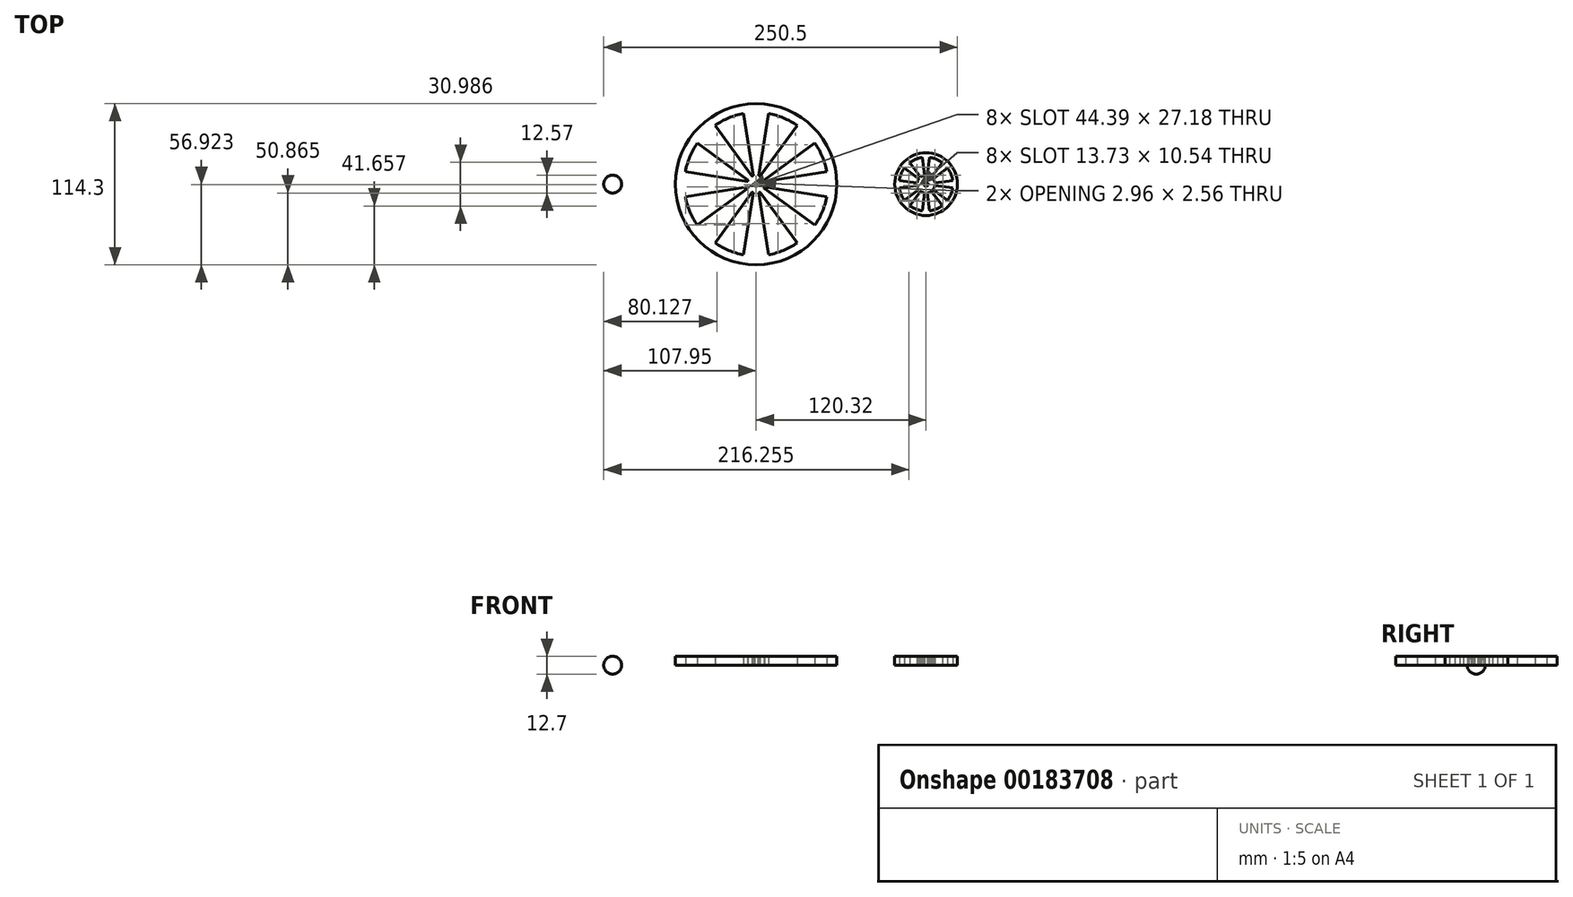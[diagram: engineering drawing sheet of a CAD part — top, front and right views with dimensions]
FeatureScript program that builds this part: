
annotation { "Feature Type Name" : "Feature", "Feature Type Description" : "" }
export const myFeature = defineFeature(function(context is Context, id is Id, definition is map)
    precondition{}
    {
        {
            var Q0;
            Q0=qCreatedBy(makeId("Top.planeOp"),FACE);
            var sketch = newSketch(context, id + "F0", { "sketchPlane" : qUnion([Q0])});
            skCircle(sketch, "E0", {"center": v(0, 0) * mm, "radius": 1.5 * mm});
            skCircle(sketch, "E1", {"center": v(0, 0) * mm, "radius": 57.15 * mm});
            skCircle(sketch, "E2", {"center": v(0, 0) * mm, "radius": 6.35 * mm});
            skCircle(sketch, "E3", {"center": v(0, 0) * mm, "radius": 50.8 * mm});
            skLineSegment(sketch, "E4", {"start": v(0, 6.35) * mm, "end": v(0, 50.8) * mm, "construction": true});
            skLineSegment(sketch, "E5", {"start": v(-1.9, 6.06) * mm, "end": v(-8.9, 50.02) * mm});
            skLineSegment(sketch, "E6", {"start": v(8.89, 50.02) * mm, "end": v(1.9, 6.06) * mm});
            skLineSegment(sketch, "E7.1.0", {"start": v(-29.08, 41.65) * mm, "end": v(-2.94, 5.63) * mm});
            skLineSegment(sketch, "E7.1.1", {"start": v(-5.63, 2.94) * mm, "end": v(-41.65, 29.08) * mm});
            skLineSegment(sketch, "E7.2.0", {"start": v(-50.02, 8.9) * mm, "end": v(-6.06, 1.9) * mm});
            skLineSegment(sketch, "E7.2.1", {"start": v(-6.06, -1.9) * mm, "end": v(-50.02, -8.9) * mm});
            skLineSegment(sketch, "E7.3.0", {"start": v(-41.65, -29.08) * mm, "end": v(-5.63, -2.94) * mm});
            skLineSegment(sketch, "E7.3.1", {"start": v(-2.94, -5.63) * mm, "end": v(-29.08, -41.65) * mm});
            skLineSegment(sketch, "E7.4.0", {"start": v(-8.9, -50.02) * mm, "end": v(-1.9, -6.06) * mm});
            skLineSegment(sketch, "E7.4.1", {"start": v(1.9, -6.06) * mm, "end": v(8.9, -50.02) * mm});
            skLineSegment(sketch, "E7.5.0", {"start": v(29.08, -41.65) * mm, "end": v(2.94, -5.63) * mm});
            skLineSegment(sketch, "E7.5.1", {"start": v(5.63, -2.94) * mm, "end": v(41.65, -29.08) * mm});
            skLineSegment(sketch, "E7.6.0", {"start": v(50.02, -8.9) * mm, "end": v(6.06, -1.9) * mm});
            skLineSegment(sketch, "E7.6.1", {"start": v(6.06, 1.9) * mm, "end": v(50.02, 8.9) * mm});
            skLineSegment(sketch, "E7.7.0", {"start": v(41.65, 29.08) * mm, "end": v(5.63, 2.94) * mm});
            skLineSegment(sketch, "E7.7.1", {"start": v(2.94, 5.63) * mm, "end": v(29.08, 41.65) * mm});
            skCircle(sketch, "E8", {"center": v(120.32, 0) * mm, "radius": 6.35 * mm});
            skCircle(sketch, "E9", {"center": v(120.32, 0) * mm, "radius": 1.5 * mm});
            skCircle(sketch, "E10", {"center": v(120.32, 0) * mm, "radius": 22.23 * mm});
            skCircle(sketch, "E11", {"center": v(120.32, 0) * mm, "radius": 19.05 * mm});
            skLineSegment(sketch, "E12", {"start": v(120.32, 6.35) * mm, "end": v(120.32, 19.05) * mm, "construction": true});
            skLineSegment(sketch, "E13", {"start": v(121.34, 6.27) * mm, "end": v(122.86, 18.88) * mm});
            skLineSegment(sketch, "E14", {"start": v(119.3, 6.27) * mm, "end": v(117.78, 18.88) * mm});
            skLineSegment(sketch, "E15.1.0", {"start": v(116.6, 5.15) * mm, "end": v(108.77, 15.15) * mm});
            skLineSegment(sketch, "E15.1.1", {"start": v(115.17, 3.71) * mm, "end": v(105.17, 11.55) * mm});
            skLineSegment(sketch, "E15.2.0", {"start": v(114.05, 1.02) * mm, "end": v(101.44, 2.54) * mm});
            skLineSegment(sketch, "E15.2.1", {"start": v(114.05, -1.02) * mm, "end": v(101.44, -2.54) * mm});
            skLineSegment(sketch, "E15.3.0", {"start": v(115.17, -3.71) * mm, "end": v(105.17, -11.55) * mm});
            skLineSegment(sketch, "E15.3.1", {"start": v(116.6, -5.15) * mm, "end": v(108.77, -15.15) * mm});
            skLineSegment(sketch, "E15.4.0", {"start": v(119.3, -6.27) * mm, "end": v(117.78, -18.88) * mm});
            skLineSegment(sketch, "E15.4.1", {"start": v(121.34, -6.27) * mm, "end": v(122.86, -18.88) * mm});
            skLineSegment(sketch, "E15.5.0", {"start": v(124.03, -5.15) * mm, "end": v(131.87, -15.15) * mm});
            skLineSegment(sketch, "E15.5.1", {"start": v(125.47, -3.71) * mm, "end": v(135.47, -11.55) * mm});
            skLineSegment(sketch, "E15.6.0", {"start": v(126.59, -1.02) * mm, "end": v(139.2, -2.54) * mm});
            skLineSegment(sketch, "E15.6.1", {"start": v(126.59, 1.02) * mm, "end": v(139.2, 2.54) * mm});
            skLineSegment(sketch, "E15.7.0", {"start": v(125.47, 3.71) * mm, "end": v(135.47, 11.55) * mm});
            skLineSegment(sketch, "E15.7.1", {"start": v(124.03, 5.15) * mm, "end": v(131.87, 15.15) * mm});
            skLineSegment(sketch, "E16", {"start": v(-1.08, 1.05) * mm, "end": v(1.08, 1.05) * mm});
            skPoint(sketch, "E17", {"position": v(0, 1.5) * mm});
            skLineSegment(sketch, "E18", {"start": v(119.24, 1.05) * mm, "end": v(121.4, 1.05) * mm});
            skPoint(sketch, "E19", {"position": v(120.32, 1.5) * mm});
            skCircle(sketch, "E20", {"center": v(-101.6, 0) * mm, "radius": 6.35 * mm});
            skLineSegment(sketch, "E21", {"start": v(-107.95, 0) * mm, "end": v(-95.25, 0) * mm});
            skSolve(sketch);
        }
        {
            var Q0;
            Q0=makeQuery(id+"F0.imprint","IMPRINT",FACE,{"disambiguationData":[TD([[makeQuery(id+"F0.imprint","IMPRINT",EDGE,{"derivedFrom":sQuery(id+"F0.wireOp",EDGE,"E1")}),1.0]])]});
            var Q1;
            {var subQ0=sQuery(id+"F0.wireOp",EDGE,"E7.1.1");var subQ1=sQuery(id+"F0.wireOp",EDGE,"E2");var subQ2=makeQuery(id+"F0.imprint","INTERSECT",VERTEX,{"derivedFrom":[subQ1,subQ0]});Q1=makeQuery(id+"F0.imprint","IMPRINT",FACE,{"disambiguationData":[TD([[makeQuery(id+"F0.imprint","IMPRINT",EDGE,{"disambiguationData":[TD([[subQ2,1.0]])],"derivedFrom":subQ1}),-1.0]])]});}
            var Q2;
            Q2=makeQuery(id+"F0.imprint","IMPRINT",FACE,{"disambiguationData":[TD([[makeQuery(id+"F0.imprint","IMPRINT",EDGE,{"derivedFrom":sQuery(id+"F0.wireOp",EDGE,"E0")}),-1.0]])]});
            var Q3;
            {var subQ0=sQuery(id+"F0.wireOp",EDGE,"E5");var subQ1=sQuery(id+"F0.wireOp",EDGE,"E2");var subQ2=makeQuery(id+"F0.imprint","INTERSECT",VERTEX,{"derivedFrom":[subQ1,subQ0]});Q3=makeQuery(id+"F0.imprint","IMPRINT",FACE,{"disambiguationData":[TD([[makeQuery(id+"F0.imprint","IMPRINT",EDGE,{"disambiguationData":[TD([[subQ2,1.0]])],"derivedFrom":subQ1}),-1.0]])]});}
            var Q4;
            {var subQ0=sQuery(id+"F0.wireOp",EDGE,"E6");var subQ1=sQuery(id+"F0.wireOp",EDGE,"E2");var subQ2=makeQuery(id+"F0.imprint","INTERSECT",VERTEX,{"derivedFrom":[subQ1,subQ0]});Q4=makeQuery(id+"F0.imprint","IMPRINT",FACE,{"disambiguationData":[TD([[makeQuery(id+"F0.imprint","IMPRINT",EDGE,{"disambiguationData":[TD([[subQ2,-1.0]])],"derivedFrom":subQ1}),-1.0]])]});}
            var Q5;
            {var subQ0=sQuery(id+"F0.wireOp",EDGE,"E7.6.1");var subQ1=sQuery(id+"F0.wireOp",EDGE,"E2");var subQ2=makeQuery(id+"F0.imprint","INTERSECT",VERTEX,{"derivedFrom":[subQ1,subQ0]});Q5=makeQuery(id+"F0.imprint","IMPRINT",FACE,{"disambiguationData":[TD([[makeQuery(id+"F0.imprint","IMPRINT",EDGE,{"disambiguationData":[TD([[subQ2,1.0]])],"derivedFrom":subQ1}),-1.0]])]});}
            var Q6;
            {var subQ0=sQuery(id+"F0.wireOp",EDGE,"E7.5.1");var subQ1=sQuery(id+"F0.wireOp",EDGE,"E2");var subQ2=makeQuery(id+"F0.imprint","INTERSECT",VERTEX,{"derivedFrom":[subQ1,subQ0]});Q6=makeQuery(id+"F0.imprint","IMPRINT",FACE,{"disambiguationData":[TD([[makeQuery(id+"F0.imprint","IMPRINT",EDGE,{"disambiguationData":[TD([[subQ2,1.0]])],"derivedFrom":subQ1}),-1.0]])]});}
            var Q7;
            {var subQ0=sQuery(id+"F0.wireOp",EDGE,"E7.4.1");var subQ1=sQuery(id+"F0.wireOp",EDGE,"E2");var subQ2=makeQuery(id+"F0.imprint","INTERSECT",VERTEX,{"derivedFrom":[subQ1,subQ0]});Q7=makeQuery(id+"F0.imprint","IMPRINT",FACE,{"disambiguationData":[TD([[makeQuery(id+"F0.imprint","IMPRINT",EDGE,{"disambiguationData":[TD([[subQ2,1.0]])],"derivedFrom":subQ1}),-1.0]])]});}
            var Q8;
            {var subQ0=sQuery(id+"F0.wireOp",EDGE,"E7.3.1");var subQ1=sQuery(id+"F0.wireOp",EDGE,"E2");var subQ2=makeQuery(id+"F0.imprint","INTERSECT",VERTEX,{"derivedFrom":[subQ1,subQ0]});Q8=makeQuery(id+"F0.imprint","IMPRINT",FACE,{"disambiguationData":[TD([[makeQuery(id+"F0.imprint","IMPRINT",EDGE,{"disambiguationData":[TD([[subQ2,1.0]])],"derivedFrom":subQ1}),-1.0]])]});}
            var Q9;
            {var subQ0=sQuery(id+"F0.wireOp",EDGE,"E7.2.1");var subQ1=sQuery(id+"F0.wireOp",EDGE,"E2");var subQ2=makeQuery(id+"F0.imprint","INTERSECT",VERTEX,{"derivedFrom":[subQ1,subQ0]});Q9=makeQuery(id+"F0.imprint","IMPRINT",FACE,{"disambiguationData":[TD([[makeQuery(id+"F0.imprint","IMPRINT",EDGE,{"disambiguationData":[TD([[subQ2,1.0]])],"derivedFrom":subQ1}),-1.0]])]});}
            var Q10;
            {var subQ0=sQuery(id+"F0.wireOp",EDGE,"E7.7.0");Q10=makeQuery(id+"F0.imprint","IMPRINT",FACE,{"disambiguationData":[TD([[makeQuery(id+"F0.imprint","IMPRINT",EDGE,{"derivedFrom":subQ0}),-1.0]])]});}
            var Q11;
            {var subQ0=sQuery(id+"F0.wireOp",EDGE,"E13");Q11=makeQuery(id+"F0.imprint","IMPRINT",FACE,{"disambiguationData":[TD([[makeQuery(id+"F0.imprint","IMPRINT",EDGE,{"derivedFrom":subQ0}),1.0]])]});}
            var Q12;
            Q12=makeQuery(id+"F0.imprint","IMPRINT",FACE,{"disambiguationData":[TD([[makeQuery(id+"F0.imprint","IMPRINT",EDGE,{"derivedFrom":sQuery(id+"F0.wireOp",EDGE,"E10")}),1.0]])]});
            var Q13;
            {var subQ0=sQuery(id+"F0.wireOp",EDGE,"E15.1.0");Q13=makeQuery(id+"F0.imprint","IMPRINT",FACE,{"disambiguationData":[TD([[makeQuery(id+"F0.imprint","IMPRINT",EDGE,{"derivedFrom":subQ0}),1.0]])]});}
            var Q14;
            {var subQ0=sQuery(id+"F0.wireOp",EDGE,"E15.2.0");Q14=makeQuery(id+"F0.imprint","IMPRINT",FACE,{"disambiguationData":[TD([[makeQuery(id+"F0.imprint","IMPRINT",EDGE,{"derivedFrom":subQ0}),1.0]])]});}
            var Q15;
            Q15=makeQuery(id+"F0.imprint","IMPRINT",FACE,{"disambiguationData":[TD([[makeQuery(id+"F0.imprint","IMPRINT",EDGE,{"derivedFrom":sQuery(id+"F0.wireOp",EDGE,"E9")}),-1.0]])]});
            var Q16;
            {var subQ0=sQuery(id+"F0.wireOp",EDGE,"E15.3.0");Q16=makeQuery(id+"F0.imprint","IMPRINT",FACE,{"disambiguationData":[TD([[makeQuery(id+"F0.imprint","IMPRINT",EDGE,{"derivedFrom":subQ0}),1.0]])]});}
            var Q17;
            {var subQ0=sQuery(id+"F0.wireOp",EDGE,"E15.4.0");Q17=makeQuery(id+"F0.imprint","IMPRINT",FACE,{"disambiguationData":[TD([[makeQuery(id+"F0.imprint","IMPRINT",EDGE,{"derivedFrom":subQ0}),1.0]])]});}
            var Q18;
            {var subQ0=sQuery(id+"F0.wireOp",EDGE,"E15.5.0");Q18=makeQuery(id+"F0.imprint","IMPRINT",FACE,{"disambiguationData":[TD([[makeQuery(id+"F0.imprint","IMPRINT",EDGE,{"derivedFrom":subQ0}),1.0]])]});}
            var Q19;
            {var subQ0=sQuery(id+"F0.wireOp",EDGE,"E15.6.0");Q19=makeQuery(id+"F0.imprint","IMPRINT",FACE,{"disambiguationData":[TD([[makeQuery(id+"F0.imprint","IMPRINT",EDGE,{"derivedFrom":subQ0}),1.0]])]});}
            var Q20;
            {var subQ0=sQuery(id+"F0.wireOp",EDGE,"E15.7.0");Q20=makeQuery(id+"F0.imprint","IMPRINT",FACE,{"disambiguationData":[TD([[makeQuery(id+"F0.imprint","IMPRINT",EDGE,{"derivedFrom":subQ0}),1.0]])]});}
            var Q21;
            {var subQ0=sQuery(id+"F0.wireOp",EDGE,"E18");Q21=makeQuery(id+"F0.imprint","IMPRINT",FACE,{"disambiguationData":[TD([[makeQuery(id+"F0.imprint","IMPRINT",EDGE,{"derivedFrom":subQ0}),1.0]])]});}
            var Q22;
            {var subQ0=sQuery(id+"F0.wireOp",EDGE,"E16");Q22=makeQuery(id+"F0.imprint","IMPRINT",FACE,{"disambiguationData":[TD([[makeQuery(id+"F0.imprint","IMPRINT",EDGE,{"derivedFrom":subQ0}),1.0]])]});}
            extrude(context, id + "F1", {"entities" : qUnion([Q0, Q1, Q2, Q3, Q4, Q5, Q6, Q7, Q8, Q9, Q10, Q11, Q12, Q13, Q14, Q15, Q16, Q17, Q18, Q19, Q20, Q21, Q22]), "depth" : 6.35 * mm});
        }
        {
            var Q0;
            {var subQ0=sQuery(id+"F0.wireOp",EDGE,"E21");Q0=makeQuery(id+"F0.imprint","IMPRINT",FACE,{"disambiguationData":[TD([[makeQuery(id+"F0.imprint","IMPRINT",EDGE,{"derivedFrom":subQ0}),1.0]])]});}
            var Q1;
            Q1=sQuery(id+"F0.wireOp",EDGE,"E21");
            revolve(context, id + "F2", {"entities" : qUnion([Q0]), "axis" : qUnion([Q1]), "revolveType" : RevolveType.FULL});
        }
    });
